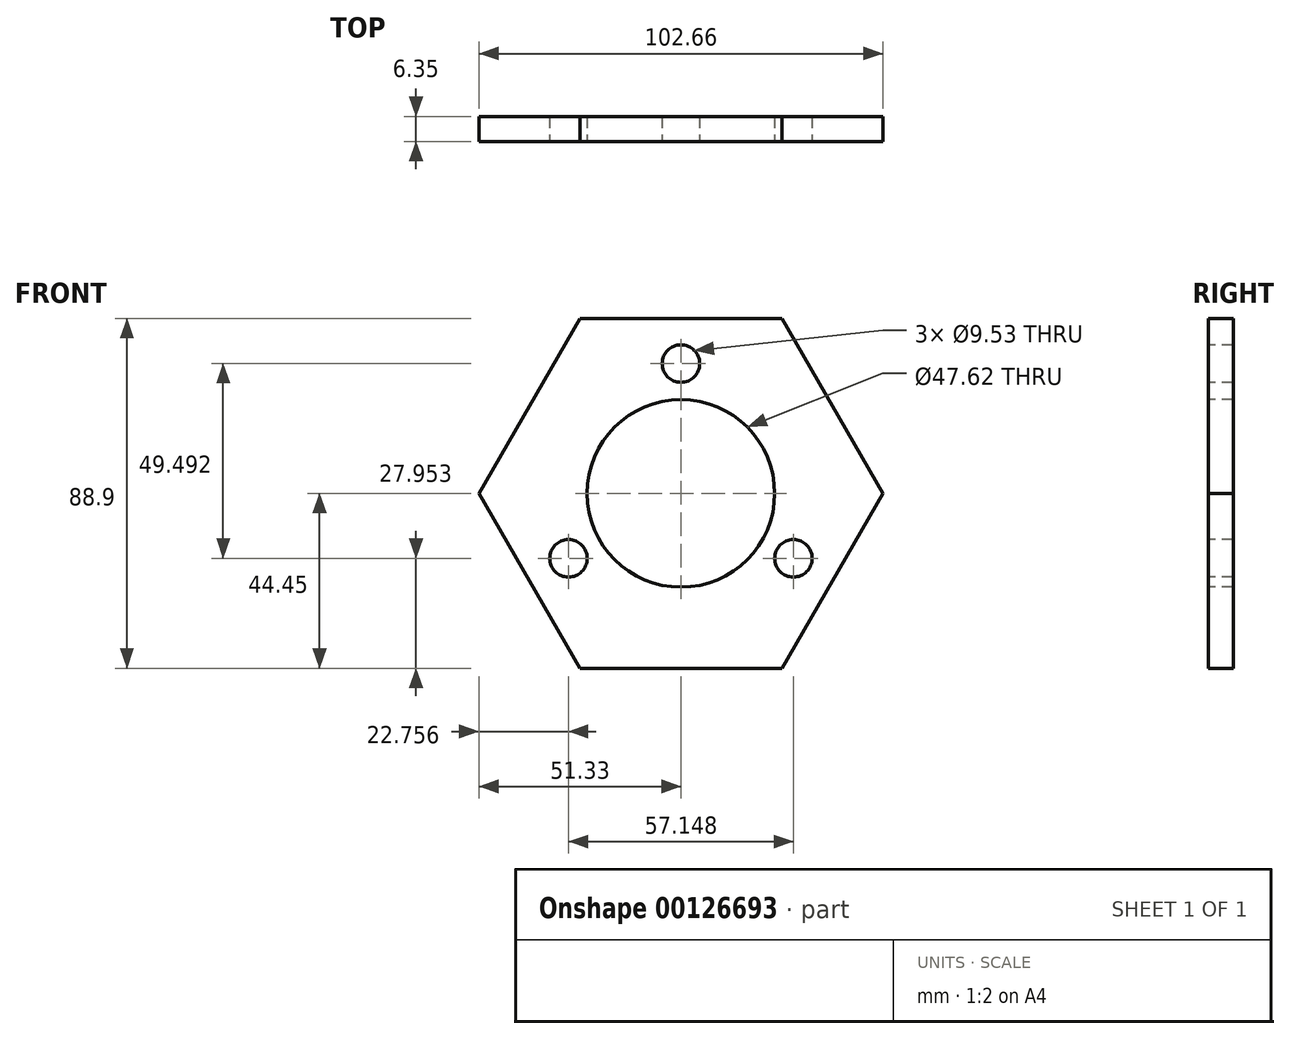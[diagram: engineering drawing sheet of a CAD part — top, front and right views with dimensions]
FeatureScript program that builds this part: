
annotation { "Feature Type Name" : "Feature", "Feature Type Description" : "" }
export const myFeature = defineFeature(function(context is Context, id is Id, definition is map)
    precondition{}
    {
        {
            var Q0;
            Q0=qCreatedBy(makeId("Front.planeOp"),FACE);
            var sketch = newSketch(context, id + "F0", { "sketchPlane" : qUnion([Q0])});
            skCircle(sketch, "E0", {"center": v(0, 0) * mm, "radius": 23.81 * mm});
            skCircle(sketch, "E1", {"center": v(0, 33) * mm, "radius": 4.76 * mm});
            skCircle(sketch, "E2.1.0", {"center": v(-28.57, -16.5) * mm, "radius": 4.76 * mm});
            skCircle(sketch, "E2.2.0", {"center": v(28.57, -16.5) * mm, "radius": 4.76 * mm});
            skCircle(sketch, "E3.cCircle", {"center": v(0, 0) * mm, "radius": 44.45 * mm, "construction": true});
            skLineSegment(sketch, "E3.0", {"start": v(-51.33, 0) * mm, "end": v(-25.66, 44.45) * mm});
            skLineSegment(sketch, "E3.1", {"start": v(-25.66, 44.45) * mm, "end": v(25.66, 44.45) * mm});
            skLineSegment(sketch, "E3.2", {"start": v(25.66, 44.45) * mm, "end": v(51.33, 0) * mm});
            skLineSegment(sketch, "E3.3", {"start": v(51.33, 0) * mm, "end": v(25.66, -44.45) * mm});
            skLineSegment(sketch, "E3.4", {"start": v(25.66, -44.45) * mm, "end": v(-25.66, -44.45) * mm});
            skLineSegment(sketch, "E3.5", {"start": v(-25.66, -44.45) * mm, "end": v(-51.33, 0) * mm});
            skPoint(sketch, "E3.0.midPoint", {"position": v(-38.5, 22.23) * mm});
            skSolve(sketch);
        }
        {
            var Q0;
            Q0 = qSketchRegion(id + "F0", true);
            extrude(context, id + "F1", {"entities" : qUnion([Q0]), "oppositeDirection" : true, "depth" : 6.35 * mm});
        }
        {
            var Q0;
            Q0=qCreatedBy(makeId("Front.planeOp"),FACE);
            cPlane(context, id + "F2", {"entities" : qUnion([Q0]), "cplaneType" : CPlaneType.OFFSET, "offset" : 101.6 * mm, "width" : 152.4 * mm, "height" : 152.4 * mm});
        }
        {
            var Q0;
            Q0=qCreatedBy(id+"F2.planeOp",FACE);
            var sketch = newSketch(context, id + "F3", { "sketchPlane" : qUnion([Q0])});
            skCircle(sketch, "E4.cCircle", {"center": v(0, 0) * mm, "radius": 25.4 * mm, "construction": true});
            skLineSegment(sketch, "E4.0", {"start": v(-14.66, 25.4) * mm, "end": v(14.66, 25.4) * mm});
            skLineSegment(sketch, "E4.1", {"start": v(14.66, 25.4) * mm, "end": v(29.33, 0) * mm});
            skLineSegment(sketch, "E4.2", {"start": v(29.33, 0) * mm, "end": v(14.66, -25.4) * mm});
            skLineSegment(sketch, "E4.3", {"start": v(14.66, -25.4) * mm, "end": v(-14.66, -25.4) * mm});
            skLineSegment(sketch, "E4.4", {"start": v(-14.66, -25.4) * mm, "end": v(-29.33, 0) * mm});
            skLineSegment(sketch, "E4.5", {"start": v(-29.33, 0) * mm, "end": v(-14.66, 25.4) * mm});
            skPoint(sketch, "E4.0.midPoint", {"position": v(0, 25.4) * mm});
            skSolve(sketch);
        }
        {
            var Q0;
            Q0=sQuery(id+"F0.wireOp",EDGE,"E3.1");
            var Q1;
            Q1=sQuery(id+"F3.wireOp",EDGE,"E4.0");
            loft(context, id + "F4", {"bodyType" : ToolBodyType.SURFACE, "wireProfilesArray" : [{ "wireProfileEntities" : qUnion([Q0]) }, { "wireProfileEntities" : qUnion([Q1]) }]});
        }
        {
            var Q0;
            Q0=sQuery(id+"F0.wireOp",EDGE,"E3.2");
            var Q1;
            Q1=sQuery(id+"F3.wireOp",EDGE,"E4.1");
            loft(context, id + "F5", {"bodyType" : ToolBodyType.SURFACE, "wireProfilesArray" : [{ "wireProfileEntities" : qUnion([Q0]) }, { "wireProfileEntities" : qUnion([Q1]) }]});
        }
        {
            var Q0;
            Q0=sQuery(id+"F0.wireOp",EDGE,"E3.3");
            var Q1;
            Q1=sQuery(id+"F3.wireOp",EDGE,"E4.2");
            loft(context, id + "F6", {"bodyType" : ToolBodyType.SURFACE, "wireProfilesArray" : [{ "wireProfileEntities" : qUnion([Q0]) }, { "wireProfileEntities" : qUnion([Q1]) }]});
        }
        {
            var Q0;
            Q0=sQuery(id+"F0.wireOp",EDGE,"E3.0");
            var Q1;
            Q1=sQuery(id+"F3.wireOp",EDGE,"E4.5");
            loft(context, id + "F7", {"bodyType" : ToolBodyType.SURFACE, "wireProfilesArray" : [{ "wireProfileEntities" : qUnion([Q0]) }, { "wireProfileEntities" : qUnion([Q1]) }]});
        }
        {
            var Q0;
            Q0=sQuery(id+"F0.wireOp",EDGE,"E3.5");
            var Q1;
            Q1=sQuery(id+"F3.wireOp",EDGE,"E4.4");
            loft(context, id + "F8", {"bodyType" : ToolBodyType.SURFACE, "wireProfilesArray" : [{ "wireProfileEntities" : qUnion([Q0]) }, { "wireProfileEntities" : qUnion([Q1]) }]});
        }
        {
            var Q0;
            Q0=sQuery(id+"F0.wireOp",EDGE,"E3.4");
            var Q1;
            Q1=sQuery(id+"F3.wireOp",EDGE,"E4.3");
            loft(context, id + "F9", {"bodyType" : ToolBodyType.SURFACE, "wireProfilesArray" : [{ "wireProfileEntities" : qUnion([Q0]) }, { "wireProfileEntities" : qUnion([Q1]) }]});
        }
    });
